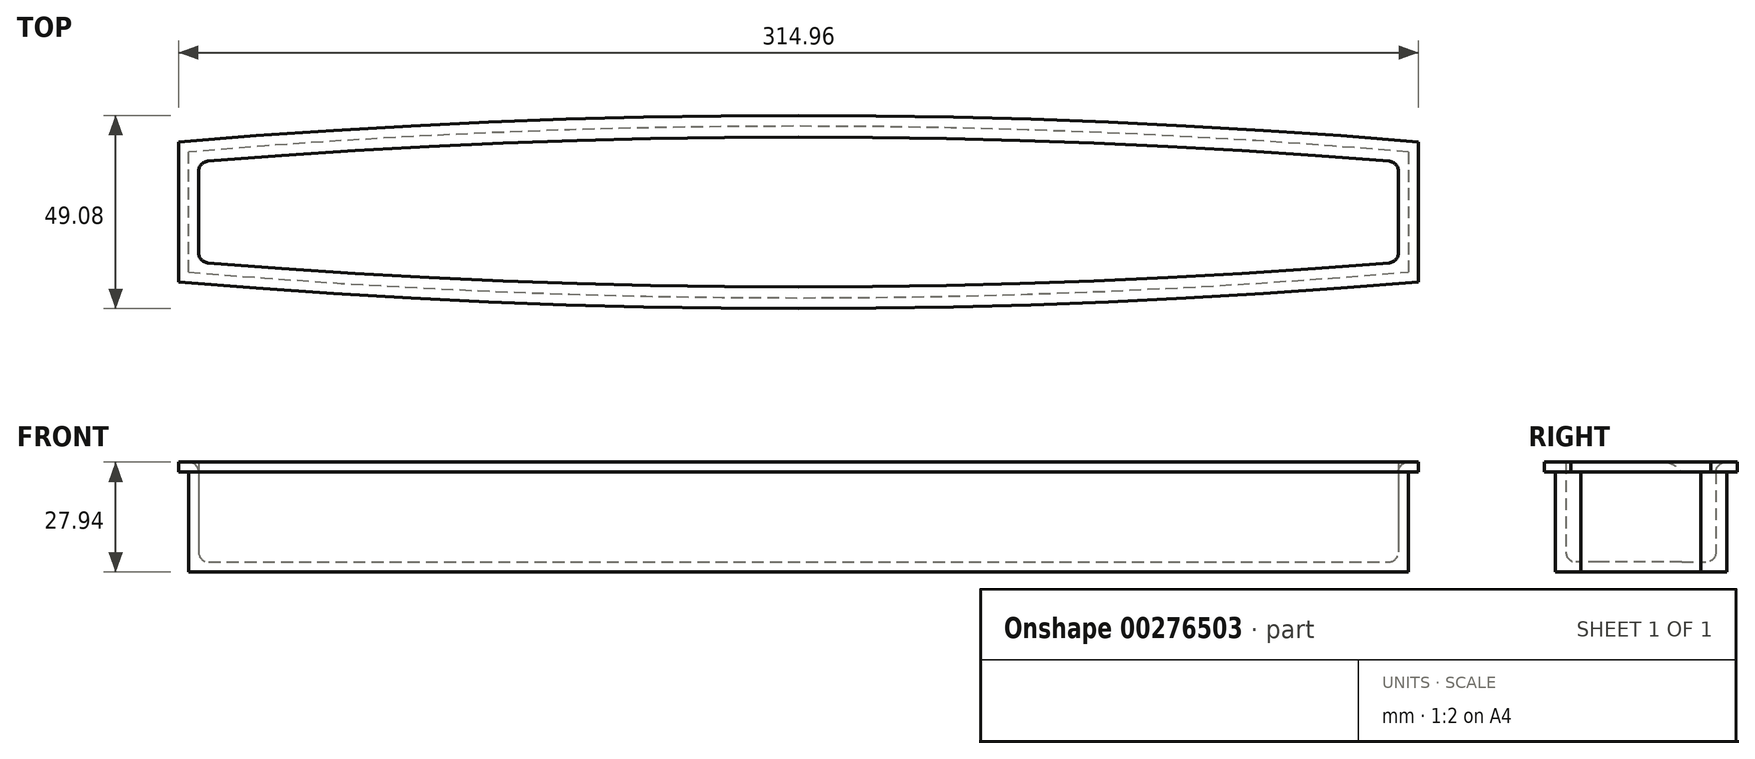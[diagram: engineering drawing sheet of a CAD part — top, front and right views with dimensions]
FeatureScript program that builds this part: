
annotation { "Feature Type Name" : "Feature", "Feature Type Description" : "" }
export const myFeature = defineFeature(function(context is Context, id is Id, definition is map)
    precondition{}
    {
        {
            var Q0;
            Q0=qCreatedBy(makeId("Top.planeOp"),FACE);
            var sketch = newSketch(context, id + "F0", { "sketchPlane" : qUnion([Q0])});
            skLineSegment(sketch, "E0", {"start": v(0, 0) * mm, "end": v(0, 25.4) * mm});
            skLineSegment(sketch, "E1", {"start": v(0, 25.4) * mm, "end": v(304.8, 25.4) * mm, "construction": true});
            skLineSegment(sketch, "E2", {"start": v(304.8, 25.4) * mm, "end": v(304.8, 0) * mm});
            skArc(sketch, "E3", {"start": v(304.8, 25.4) * mm, "mid": v(152.4, 31.75) * mm, "end": v(0, 25.4) * mm});
            skArc(sketch, "E4", {"start": v(0, 0) * mm, "mid": v(152.4, -6.35) * mm, "end": v(304.8, 0) * mm});
            skLineSegment(sketch, "E5", {"start": v(-2.54, -2.54) * mm, "end": v(-2.54, 27.94) * mm});
            skLineSegment(sketch, "E6", {"start": v(307.34, 27.94) * mm, "end": v(307.34, -2.54) * mm});
            skLineSegment(sketch, "E7", {"start": v(-2.54, 12.7) * mm, "end": v(0, 12.7) * mm, "construction": true});
            skLineSegment(sketch, "E8", {"start": v(304.8, 12.7) * mm, "end": v(307.34, 12.7) * mm, "construction": true});
            skArc(sketch, "E9", {"start": v(307.34, 27.94) * mm, "mid": v(152.4, 34.5) * mm, "end": v(-2.54, 27.94) * mm});
            skArc(sketch, "E10", {"start": v(-2.54, -2.54) * mm, "mid": v(152.4, -9.1) * mm, "end": v(307.34, -2.54) * mm});
            skSolve(sketch);
        }
        {
            var Q0;
            Q0=makeQuery(id+"F0.imprint","IMPRINT",FACE,{"disambiguationData":[TD([[makeQuery(id+"F0.imprint","IMPRINT",EDGE,{"derivedFrom":sQuery(id+"F0.wireOp",EDGE,"E0")}),-1.0]])]});
            extrude(context, id + "F1", {"entities" : qUnion([Q0]), "depth" : 2.54 * mm});
        }
        {
            var Q0;
            Q0=makeQuery(id+"F0.imprint","IMPRINT",FACE,{"disambiguationData":[TD([[makeQuery(id+"F0.imprint","IMPRINT",EDGE,{"derivedFrom":sQuery(id+"F0.wireOp",EDGE,"E0")}),1.0]])]});
            extrude(context, id + "F2", {"entities" : qUnion([Q0]), "operationType" : NewBodyOperationType.ADD, "depth" : 27.94 * mm});
        }
        {
            var Q0;
            Q0=makeQuery(id+"F2.opExtrude","CAP_FACE",FACE,{"disambiguationData":[OSD([sQuery(id+"F0.wireOp",EDGE,"E0"),sQuery(id+"F0.wireOp",EDGE,"E2"),sQuery(id+"F0.wireOp",EDGE,"E3"),sQuery(id+"F0.wireOp",EDGE,"E4"),sQuery(id+"F0.wireOp",EDGE,"E5"),sQuery(id+"F0.wireOp",EDGE,"E6"),sQuery(id+"F0.wireOp",EDGE,"E9"),sQuery(id+"F0.wireOp",EDGE,"E10")])],"isStart":false});
            var sketch = newSketch(context, id + "F3", { "sketchPlane" : qUnion([Q0])});
            skLineSegment(sketch, "E11", {"start": v(-5.08, 30.48) * mm, "end": v(-5.08, -5.08) * mm});
            skLineSegment(sketch, "E12", {"start": v(309.88, 30.48) * mm, "end": v(309.88, -5.08) * mm});
            skLineSegment(sketch, "E13", {"start": v(-2.54, 12.7) * mm, "end": v(-5.08, 12.7) * mm, "construction": true});
            skLineSegment(sketch, "E14", {"start": v(307.34, 12.7) * mm, "end": v(309.88, 12.7) * mm, "construction": true});
            skArc(sketch, "E15", {"start": v(309.88, 30.48) * mm, "mid": v(152.4, 37.24) * mm, "end": v(-5.08, 30.48) * mm});
            skArc(sketch, "E16", {"start": v(-5.08, -5.08) * mm, "mid": v(152.4, -11.84) * mm, "end": v(309.88, -5.08) * mm});
            skSolve(sketch);
        }
        {
            var Q0;
            Q0=makeQuery(id+"F3.imprint","IMPRINT",FACE,{"disambiguationData":[TD([[makeQuery(id+"F3.imprint","IMPRINT",EDGE,{"derivedFrom":sQuery(id+"F3.wireOp",EDGE,"E11")}),1.0]])]});
            extrude(context, id + "F4", {"entities" : qUnion([Q0]), "operationType" : NewBodyOperationType.ADD, "oppositeDirection" : true, "depth" : 2.54 * mm});
        }
        {
            var Q0;
            Q0=makeQuery(id+"F4.opExtrude","CAP_EDGE",EDGE,{"disambiguationData":[OSD([sQuery(id+"F0.wireOp",EDGE,"E10")])],"isStart":false});
            var Q1;
            Q1=makeQuery(id+"F4.opExtrude","CAP_EDGE",EDGE,{"disambiguationData":[OSD([sQuery(id+"F0.wireOp",EDGE,"E6")])],"isStart":false});
            var Q2;
            Q2=makeQuery(id+"F4.opExtrude","CAP_EDGE",EDGE,{"disambiguationData":[OSD([sQuery(id+"F0.wireOp",EDGE,"E9")])],"isStart":false});
            var Q3;
            Q3=makeQuery(id+"F4.opExtrude","CAP_EDGE",EDGE,{"disambiguationData":[OSD([sQuery(id+"F0.wireOp",EDGE,"E5")])],"isStart":false});
            var Q4;
            Q4=makeQuery(id+"F2.opExtrude","SWEPT_EDGE",EDGE,{"disambiguationData":[OSD([sQuery(id+"F0.wireOp",EDGE,"E0"),sQuery(id+"F0.wireOp",EDGE,"E3")])]});
            var Q5;
            Q5=makeQuery(id+"F1.opExtrude","CAP_EDGE",EDGE,{"disambiguationData":[OSD([sQuery(id+"F0.wireOp",EDGE,"E3")])],"isStart":false});
            var Q6;
            Q6=makeQuery(id+"F1.opExtrude","CAP_EDGE",EDGE,{"disambiguationData":[OSD([sQuery(id+"F0.wireOp",EDGE,"E0")])],"isStart":false});
            var Q7;
            Q7=makeQuery(id+"F2.opExtrude","SWEPT_EDGE",EDGE,{"disambiguationData":[OSD([sQuery(id+"F0.wireOp",EDGE,"E0"),sQuery(id+"F0.wireOp",EDGE,"E4")])]});
            var Q8;
            Q8=makeQuery(id+"F1.opExtrude","CAP_FACE",FACE,{"disambiguationData":[OSD([sQuery(id+"F0.wireOp",EDGE,"E0"),sQuery(id+"F0.wireOp",EDGE,"E2"),sQuery(id+"F0.wireOp",EDGE,"E3"),sQuery(id+"F0.wireOp",EDGE,"E4")])],"isStart":false});
            var Q9;
            Q9=makeQuery(id+"F2.opExtrude","SWEPT_EDGE",EDGE,{"disambiguationData":[OSD([sQuery(id+"F0.wireOp",EDGE,"E2"),sQuery(id+"F0.wireOp",EDGE,"E3")])]});
            var Q10;
            Q10=makeQuery(id+"F2.opExtrude","SWEPT_EDGE",EDGE,{"disambiguationData":[OSD([sQuery(id+"F0.wireOp",EDGE,"E2"),sQuery(id+"F0.wireOp",EDGE,"E4")])]});
            var Q11;
            Q11=makeQuery(id+"F2.opExtrude","CAP_EDGE",EDGE,{"disambiguationData":[OSD([sQuery(id+"F0.wireOp",EDGE,"E3")])],"isStart":false});
            fillet(context, id + "F5", {"entities" : qUnion([Q0, Q1, Q2, Q3, Q4, Q5, Q6, Q7, Q8, Q9, Q10, Q11]), "radius" : 2.54 * mm, "tangentPropagation" : true, "allowEdgeOverflow" : false});
        }
    });
